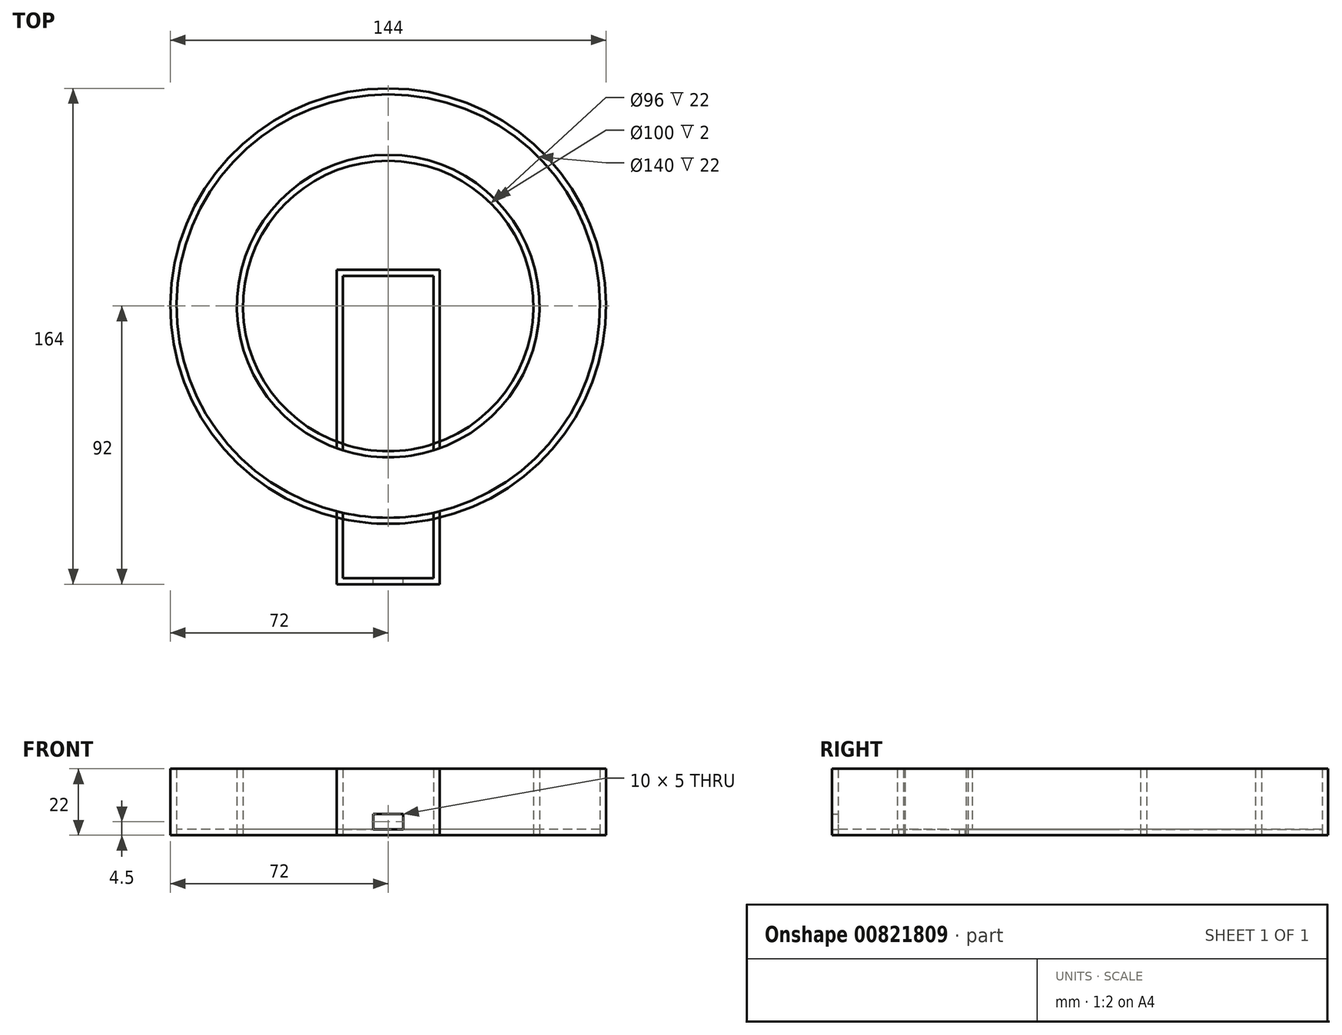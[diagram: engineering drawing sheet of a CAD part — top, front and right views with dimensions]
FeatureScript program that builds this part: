
annotation { "Feature Type Name" : "Feature", "Feature Type Description" : "" }
export const myFeature = defineFeature(function(context is Context, id is Id, definition is map)
    precondition{}
    {
        {
            var Q0;
            Q0=qCreatedBy(makeId("Top.planeOp"),FACE);
            var sketch = newSketch(context, id + "F0", { "sketchPlane" : qUnion([Q0])});
            skCircle(sketch, "E0", {"center": v(0, 0) * mm, "radius": 48 * mm});
            skCircle(sketch, "E1", {"center": v(0, 0) * mm, "radius": 50 * mm});
            skCircle(sketch, "E2", {"center": v(0, 0) * mm, "radius": 70 * mm});
            skCircle(sketch, "E3", {"center": v(0, 0) * mm, "radius": 72 * mm});
            skSolve(sketch);
        }
        {
            var Q0;
            Q0=makeQuery(id+"F0.imprint","IMPRINT",FACE,{"disambiguationData":[TD([[makeQuery(id+"F0.imprint","IMPRINT",EDGE,{"derivedFrom":sQuery(id+"F0.wireOp",EDGE,"E2")}),-1.0]])]});
            var Q1;
            Q1=makeQuery(id+"F0.imprint","IMPRINT",FACE,{"disambiguationData":[TD([[makeQuery(id+"F0.imprint","IMPRINT",EDGE,{"derivedFrom":sQuery(id+"F0.wireOp",EDGE,"E0")}),-1.0]])]});
            extrude(context, id + "F1", {"entities" : qUnion([Q0, Q1]), "depth" : 22 * mm, "offsetDistance" : 25 * mm});
        }
        {
            var Q0;
            Q0=qCreatedBy(makeId("Top.planeOp"),FACE);
            var sketch = newSketch(context, id + "F2", { "sketchPlane" : qUnion([Q0])});
            skCircle(sketch, "E4", {"center": v(0, 0) * mm, "radius": 50 * mm});
            skCircle(sketch, "E5", {"center": v(0, 0) * mm, "radius": 70 * mm});
            skSolve(sketch);
        }
        {
            var Q0;
            Q0=makeQuery(id+"F2.imprint","IMPRINT",FACE,{"disambiguationData":[TD([[makeQuery(id+"F2.imprint","IMPRINT",EDGE,{"derivedFrom":sQuery(id+"F2.wireOp",EDGE,"E4")}),-1.0]])]});
            extrude(context, id + "F3", {"entities" : qUnion([Q0]), "depth" : 2 * mm, "offsetDistance" : 25 * mm});
        }
        {
            var Q0;
            Q0=qCreatedBy(makeId("Top.planeOp"),FACE);
            var sketch = newSketch(context, id + "F4", { "sketchPlane" : qUnion([Q0])});
            skLineSegment(sketch, "E6.bottom", {"start": v(-15, 10) * mm, "end": v(15, 10) * mm});
            skLineSegment(sketch, "E6.top", {"start": v(-15, -90) * mm, "end": v(15, -90) * mm});
            skLineSegment(sketch, "E6.left", {"start": v(-15, 10) * mm, "end": v(-15, -90) * mm});
            skLineSegment(sketch, "E6.right", {"start": v(15, 10) * mm, "end": v(15, -90) * mm});
            skPoint(sketch, "E6.middle", {"position": v(0, -40) * mm});
            skLineSegment(sketch, "E7.bottom", {"start": v(-17, 12) * mm, "end": v(17, 12) * mm});
            skLineSegment(sketch, "E7.top", {"start": v(-17, -92) * mm, "end": v(17, -92) * mm});
            skLineSegment(sketch, "E7.left", {"start": v(-17, 12) * mm, "end": v(-17, -92) * mm});
            skLineSegment(sketch, "E7.right", {"start": v(17, 12) * mm, "end": v(17, -92) * mm});
            skSolve(sketch);
        }
        {
            var Q0;
            Q0=makeQuery(id+"F4.imprint","IMPRINT",FACE,{"disambiguationData":[TD([[makeQuery(id+"F4.imprint","IMPRINT",EDGE,{"derivedFrom":sQuery(id+"F4.wireOp",EDGE,"E6.bottom")}),1.0]])]});
            extrude(context, id + "F5", {"entities" : qUnion([Q0]), "depth" : 22 * mm, "offsetDistance" : 25 * mm});
        }
        {
            var Q0;
            Q0=qCreatedBy(makeId("Top.planeOp"),FACE);
            var sketch = newSketch(context, id + "F6", { "sketchPlane" : qUnion([Q0])});
            skLineSegment(sketch, "E8.bottom", {"start": v(-15, 10) * mm, "end": v(15, 10) * mm});
            skLineSegment(sketch, "E8.top", {"start": v(-15, -90) * mm, "end": v(15, -90) * mm});
            skLineSegment(sketch, "E8.left", {"start": v(-15, 10) * mm, "end": v(-15, -90) * mm});
            skLineSegment(sketch, "E8.right", {"start": v(15, 10) * mm, "end": v(15, -90) * mm});
            skPoint(sketch, "E8.middle", {"position": v(0, -40) * mm});
            skSolve(sketch);
        }
        {
            var Q0;
            Q0=makeQuery(id+"F6.imprint","IMPRINT",FACE,{"disambiguationData":[TD([[makeQuery(id+"F6.imprint","IMPRINT",EDGE,{"derivedFrom":sQuery(id+"F6.wireOp",EDGE,"E8.bottom")}),-1.0]])]});
            extrude(context, id + "F7", {"entities" : qUnion([Q0]), "depth" : 2 * mm, "offsetDistance" : 25 * mm});
        }
        {
            var Q0;
            Q0=qCreatedBy(makeId("Front.planeOp"),FACE);
            var sketch = newSketch(context, id + "F8", { "sketchPlane" : qUnion([Q0])});
            skLineSegment(sketch, "E9.bottom", {"start": v(-15, 22) * mm, "end": v(15, 22) * mm});
            skLineSegment(sketch, "E9.top", {"start": v(-15, 2) * mm, "end": v(15, 2) * mm});
            skLineSegment(sketch, "E9.left", {"start": v(-15, 22) * mm, "end": v(-15, 2) * mm});
            skLineSegment(sketch, "E9.right", {"start": v(15, 22) * mm, "end": v(15, 2) * mm});
            skPoint(sketch, "E9.middle", {"position": v(0, 12) * mm});
            skSolve(sketch);
        }
        {
            var Q0;
            Q0=makeQuery(id+"F8.imprint","IMPRINT",FACE,{"disambiguationData":[TD([[makeQuery(id+"F8.imprint","IMPRINT",EDGE,{"derivedFrom":sQuery(id+"F8.wireOp",EDGE,"E9.bottom")}),-1.0]])]});
            extrude(context, id + "F9", {"entities" : qUnion([Q0]), "operationType" : NewBodyOperationType.REMOVE, "depth" : 75 * mm, "offsetDistance" : 25 * mm});
        }
        {
            var Q0;
            Q0=qCreatedBy(makeId("Front.planeOp"),FACE);
            var sketch = newSketch(context, id + "F10", { "sketchPlane" : qUnion([Q0])});
            skLineSegment(sketch, "E10.bottom", {"start": v(-5, 7) * mm, "end": v(5, 7) * mm});
            skLineSegment(sketch, "E10.top", {"start": v(-5, 2) * mm, "end": v(5, 2) * mm});
            skLineSegment(sketch, "E10.left", {"start": v(-5, 7) * mm, "end": v(-5, 2) * mm});
            skLineSegment(sketch, "E10.right", {"start": v(5, 7) * mm, "end": v(5, 2) * mm});
            skPoint(sketch, "E10.middle", {"position": v(0, 4.5) * mm});
            skSolve(sketch);
        }
        {
            var Q0;
            Q0=makeQuery(id+"F10.imprint","IMPRINT",FACE,{"disambiguationData":[TD([[makeQuery(id+"F10.imprint","IMPRINT",EDGE,{"derivedFrom":sQuery(id+"F10.wireOp",EDGE,"E10.bottom")}),-1.0]])]});
            extrude(context, id + "F11", {"entities" : qUnion([Q0]), "operationType" : NewBodyOperationType.REMOVE, "depth" : 100 * mm, "offsetDistance" : 25 * mm});
        }
        {
            var Q0;
            Q0=qCreatedBy(makeId("Top.planeOp"),FACE);
            var sketch = newSketch(context, id + "F12", { "sketchPlane" : qUnion([Q0])});
            skCircle(sketch, "E11", {"center": v(0, 0) * mm, "radius": 50 * mm});
            skCircle(sketch, "E12", {"center": v(0, 0) * mm, "radius": 70 * mm});
            skSolve(sketch);
        }
        {
            var Q0;
            Q0 = qSketchRegion(id + "F12", true);
            var Q1;
            Q1=makeQuery(id+"F3.opExtrude","CAP_FACE",FACE,{"disambiguationData":[OSD([sQuery(id+"F2.wireOp",EDGE,"E4"),sQuery(id+"F2.wireOp",EDGE,"E5")])],"isStart":false});
            extrude(context, id + "F13", {"entities" : qUnion([Q0, Q1]), "operationType" : NewBodyOperationType.REMOVE, "depth" : 25 * mm, "offsetDistance" : 25 * mm});
        }
        {
            var Q0;
            Q0=qCreatedBy(makeId("Top.planeOp"),FACE);
            var sketch = newSketch(context, id + "F14", { "sketchPlane" : qUnion([Q0])});
            skCircle(sketch, "E13", {"center": v(0, 0) * mm, "radius": 50 * mm});
            skCircle(sketch, "E14", {"center": v(0, 0) * mm, "radius": 70 * mm});
            skSolve(sketch);
        }
        {
            var Q0;
            Q0=makeQuery(id+"F14.imprint","IMPRINT",FACE,{"disambiguationData":[TD([[makeQuery(id+"F14.imprint","IMPRINT",EDGE,{"derivedFrom":sQuery(id+"F14.wireOp",EDGE,"E13")}),-1.0]])]});
            extrude(context, id + "F15", {"entities" : qUnion([Q0]), "depth" : 2 * mm, "offsetDistance" : 25 * mm});
        }
    });
